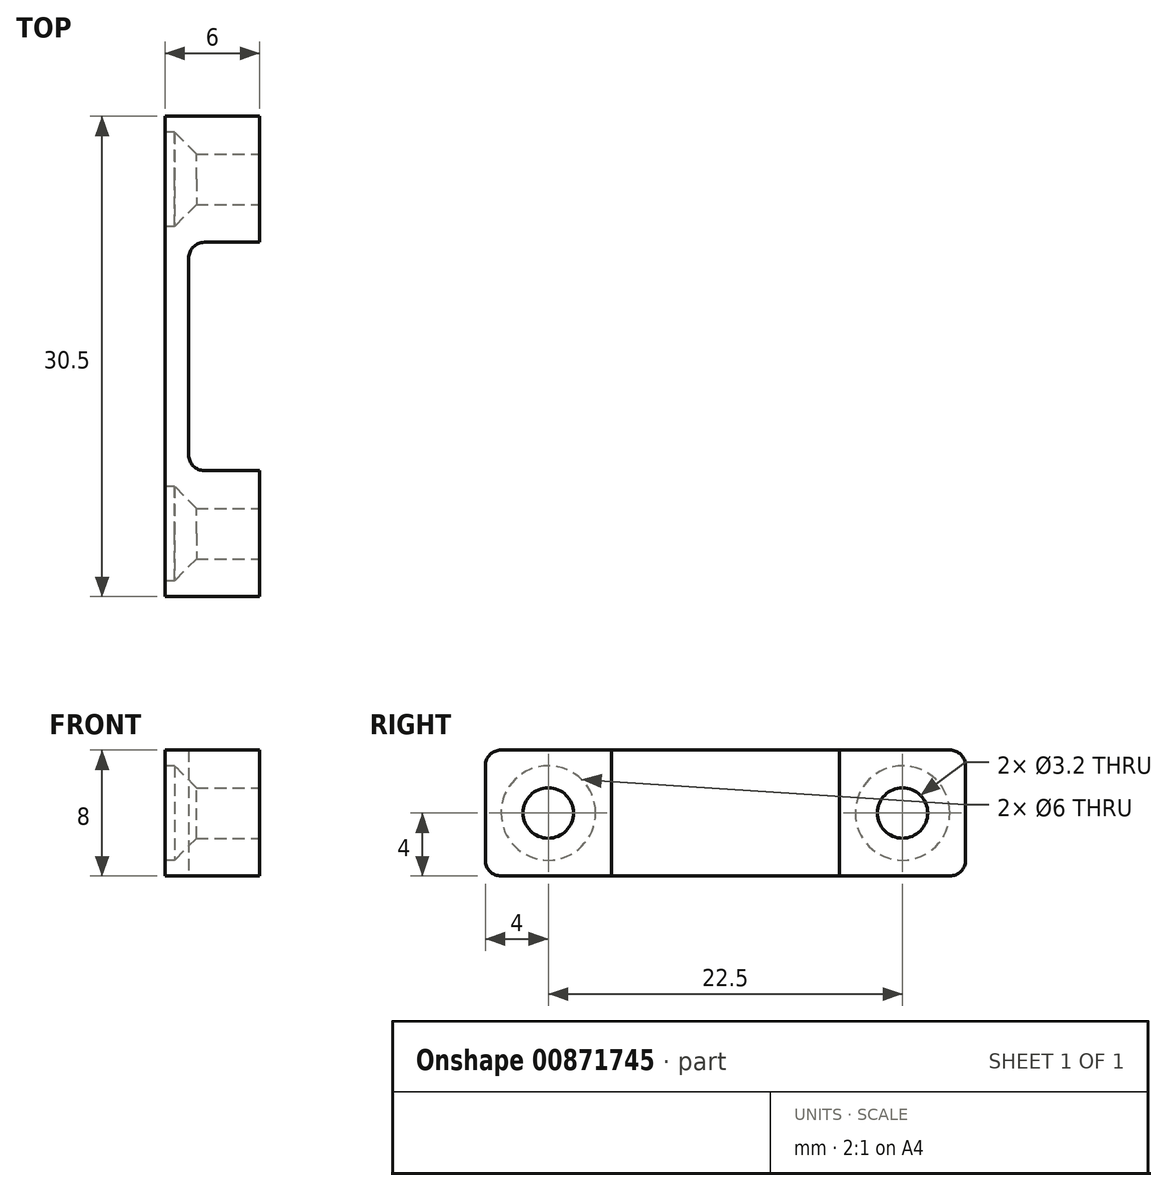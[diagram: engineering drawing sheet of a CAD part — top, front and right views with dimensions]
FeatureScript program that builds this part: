
annotation { "Feature Type Name" : "Feature", "Feature Type Description" : "" }
export const myFeature = defineFeature(function(context is Context, id is Id, definition is map)
    precondition{}
    {
        {
            var Q0;
            Q0=qCreatedBy(makeId("Top.planeOp"),FACE);
            var sketch = newSketch(context, id + "F0", { "sketchPlane" : qUnion([Q0])});
            skLineSegment(sketch, "E0", {"start": v(0, -7.25) * mm, "end": v(0, 7.25) * mm});
            skLineSegment(sketch, "E1", {"start": v(0, 7.25) * mm, "end": v(4.5, 7.25) * mm});
            skLineSegment(sketch, "E2", {"start": v(4.5, 7.25) * mm, "end": v(4.5, 15.25) * mm});
            skLineSegment(sketch, "E3", {"start": v(4.5, 15.25) * mm, "end": v(-1.5, 15.25) * mm});
            skLineSegment(sketch, "E4", {"start": v(-1.5, 15.25) * mm, "end": v(-1.5, -15.25) * mm});
            skLineSegment(sketch, "E5", {"start": v(-1.5, -15.25) * mm, "end": v(4.5, -15.25) * mm});
            skLineSegment(sketch, "E6", {"start": v(4.5, -15.25) * mm, "end": v(4.5, -7.25) * mm});
            skLineSegment(sketch, "E7", {"start": v(4.5, -7.25) * mm, "end": v(0, -7.25) * mm});
            skSolve(sketch);
        }
        {
            var Q0;
            Q0=makeQuery(id+"F0.imprint","IMPRINT",FACE,{"disambiguationData":[TD([[makeQuery(id+"F0.imprint","IMPRINT",EDGE,{"derivedFrom":sQuery(id+"F0.wireOp",EDGE,"E0")}),1.0]])]});
            extrude(context, id + "F1", {"entities" : qUnion([Q0]), "endBound" : BoundingType.SYMMETRIC, "depth" : 8 * mm, "offsetDistance" : 25 * mm});
        }
        {
            var Q0;
            Q0=makeQuery(id+"F1.opExtrude","SWEPT_FACE",FACE,{"disambiguationData":[OSD([sQuery(id+"F0.wireOp",EDGE,"E2")])]});
            var sketch = newSketch(context, id + "F2", { "sketchPlane" : qUnion([Q0])});
            skCircle(sketch, "E8", {"center": v(11.25, 0) * mm, "radius": 1.6 * mm});
            skCircle(sketch, "E9", {"center": v(-11.25, 0) * mm, "radius": 1.6 * mm});
            skSolve(sketch);
        }
        {
            var Q0;
            Q0 = qSketchRegion(id + "F2", true);
            extrude(context, id + "F3", {"entities" : qUnion([Q0]), "operationType" : NewBodyOperationType.REMOVE, "endBound" : BoundingType.THROUGH_ALL, "oppositeDirection" : true, "depth" : 25 * mm, "offsetDistance" : 25 * mm});
        }
        {
            var Q0;
            Q0=makeQuery(id+"F1.opExtrude","SWEPT_FACE",FACE,{"disambiguationData":[OSD([sQuery(id+"F0.wireOp",EDGE,"E4")])]});
            var sketch = newSketch(context, id + "F4", { "sketchPlane" : qUnion([Q0])});
            skCircle(sketch, "E10", {"center": v(-11.25, 0) * mm, "radius": 3 * mm});
            skCircle(sketch, "E11", {"center": v(11.25, 0) * mm, "radius": 3 * mm});
            skSolve(sketch);
        }
        {
            var Q0;
            Q0 = qSketchRegion(id + "F4", true);
            extrude(context, id + "F5", {"entities" : qUnion([Q0]), "operationType" : NewBodyOperationType.REMOVE, "oppositeDirection" : true, "depth" : 0.5 * mm, "offsetDistance" : 25 * mm});
        }
        {
            var Q0;
            Q0=makeQuery(id+"F5.boolean.opBoolean","INTERSECT",EDGE,{"derivedFrom":[makeQuery(id+"F3.boolean.opBoolean","COPY",FACE,{"derivedFrom":makeQuery(id+"F3.opExtrude","SWEPT_FACE",FACE,{"disambiguationData":[OSD([sQuery(id+"F2.wireOp",EDGE,"E8")])]})}),makeQuery(id+"F5.opExtrude","CAP_FACE",FACE,{"disambiguationData":[OSD([sQuery(id+"F4.wireOp",EDGE,"E10")])],"isStart":false})]});
            var Q1;
            Q1=makeQuery(id+"F5.boolean.opBoolean","INTERSECT",EDGE,{"derivedFrom":[makeQuery(id+"F3.boolean.opBoolean","COPY",FACE,{"derivedFrom":makeQuery(id+"F3.opExtrude","SWEPT_FACE",FACE,{"disambiguationData":[OSD([sQuery(id+"F2.wireOp",EDGE,"E9")])]})}),makeQuery(id+"F5.opExtrude","CAP_FACE",FACE,{"disambiguationData":[OSD([sQuery(id+"F4.wireOp",EDGE,"E11")])],"isStart":false})]});
            chamfer(context, id + "F6", {"entities" : qUnion([Q0, Q1]), "width" : 1.5 * mm, "tangentPropagation" : true});
        }
        {
            var Q0;
            Q0=makeQuery(id+"F1.opExtrude","CAP_EDGE",EDGE,{"disambiguationData":[OSD([sQuery(id+"F0.wireOp",EDGE,"E3")])],"isStart":false});
            var Q1;
            Q1=makeQuery(id+"F1.opExtrude","CAP_EDGE",EDGE,{"disambiguationData":[OSD([sQuery(id+"F0.wireOp",EDGE,"E3")])],"isStart":true});
            var Q2;
            Q2=makeQuery(id+"F1.opExtrude","CAP_EDGE",EDGE,{"disambiguationData":[OSD([sQuery(id+"F0.wireOp",EDGE,"E5")])],"isStart":false});
            var Q3;
            Q3=makeQuery(id+"F1.opExtrude","CAP_EDGE",EDGE,{"disambiguationData":[OSD([sQuery(id+"F0.wireOp",EDGE,"E5")])],"isStart":true});
            var Q4;
            Q4=makeQuery(id+"F1.opExtrude","SWEPT_EDGE",EDGE,{"disambiguationData":[OSD([sQuery(id+"F0.wireOp",EDGE,"E0"),sQuery(id+"F0.wireOp",EDGE,"E1")])]});
            var Q5;
            Q5=makeQuery(id+"F1.opExtrude","SWEPT_EDGE",EDGE,{"disambiguationData":[OSD([sQuery(id+"F0.wireOp",EDGE,"E0"),sQuery(id+"F0.wireOp",EDGE,"E7")])]});
            fillet(context, id + "F7", {"entities" : qUnion([Q0, Q1, Q2, Q3, Q4, Q5]), "tangentPropagation" : true, "radius" : 1 * mm, "defaultsChanged" : false, "vertexSettings" : [], "allowEdgeOverflow" : false});
        }
    });
